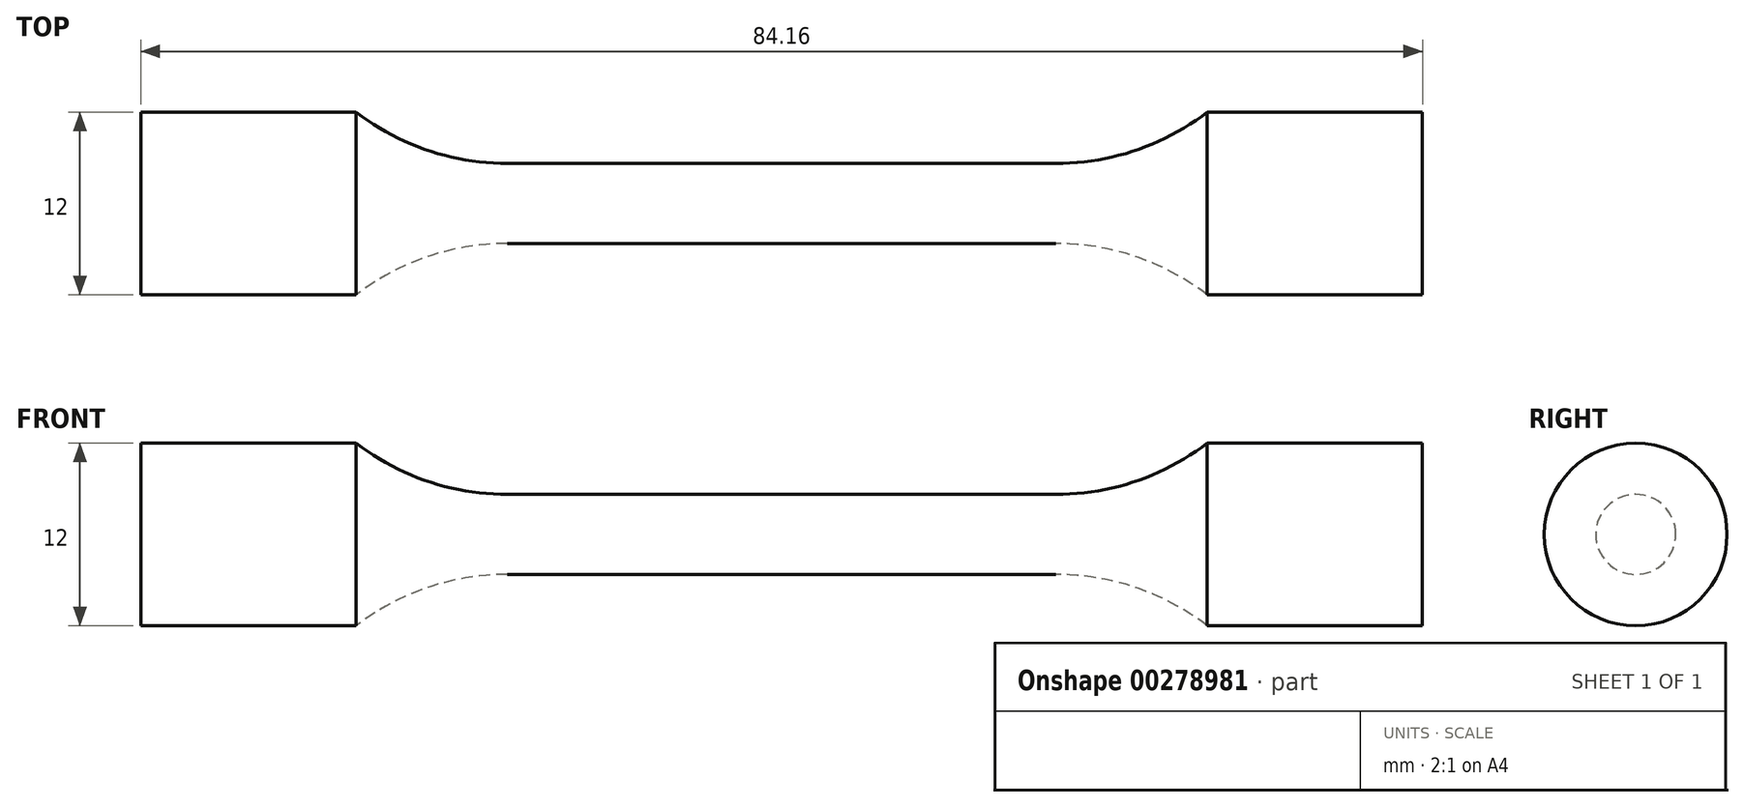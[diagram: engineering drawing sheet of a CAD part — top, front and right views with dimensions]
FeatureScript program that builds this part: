
annotation { "Feature Type Name" : "Feature", "Feature Type Description" : "" }
export const myFeature = defineFeature(function(context is Context, id is Id, definition is map)
    precondition{}
    {
        {
            var Q0;
            Q0=qCreatedBy(makeId("Front.planeOp"),FACE);
            var sketch = newSketch(context, id + "F0", { "sketchPlane" : qUnion([Q0])});
            skLineSegment(sketch, "E0", {"start": v(0, 2.63) * mm, "end": v(18, 2.63) * mm});
            skArc(sketch, "E1", {"start": v(18, 2.63) * mm, "mid": v(23.25, 3.5) * mm, "end": v(27.94, 6) * mm});
            skLineSegment(sketch, "E2", {"start": v(27.94, 6) * mm, "end": v(42.08, 6) * mm});
            skLineSegment(sketch, "E3", {"start": v(42.08, 6) * mm, "end": v(42.08, 0) * mm});
            skLineSegment(sketch, "E4.MirrorCS", {"start": v(0, 2.63) * mm, "end": v(-18, 2.63) * mm});
            skLineSegment(sketch, "E5.MirrorCS", {"start": v(-42.08, 6) * mm, "end": v(-42.08, 0) * mm});
            skLineSegment(sketch, "E6.MirrorCS", {"start": v(-27.94, 6) * mm, "end": v(-42.08, 6) * mm});
            skArc(sketch, "E7.MirrorCS", {"start": v(-18, 2.63) * mm, "mid": v(-23.25, 3.5) * mm, "end": v(-27.94, 6) * mm});
            skLineSegment(sketch, "E8", {"start": v(-42.08, 0) * mm, "end": v(42.08, 0) * mm});
            skSolve(sketch);
        }
        {
            var Q0;
            Q0 = qSketchRegion(id + "F0", true);
            var Q1;
            Q1=sQuery(id+"F0.wireOp",EDGE,"E8");
            revolve(context, id + "F1", {"entities" : qUnion([Q0]), "axis" : qUnion([Q1]), "revolveType" : RevolveType.FULL});
        }
    });
